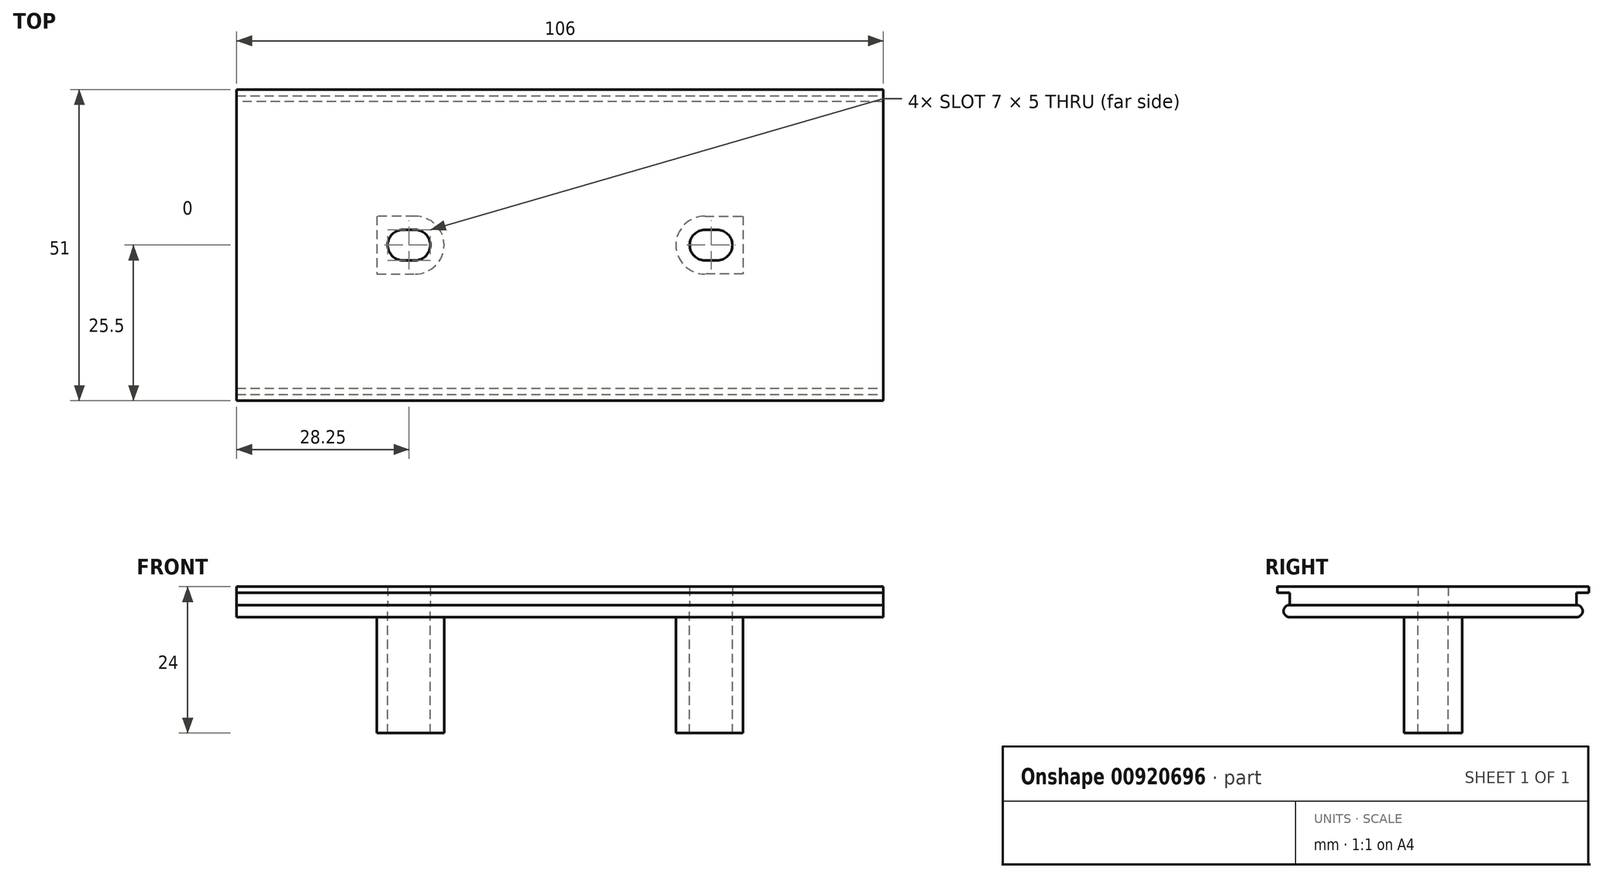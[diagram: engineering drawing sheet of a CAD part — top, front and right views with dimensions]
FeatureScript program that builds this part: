
annotation { "Feature Type Name" : "Feature", "Feature Type Description" : "" }
export const myFeature = defineFeature(function(context is Context, id is Id, definition is map)
    precondition{}
    {
        {
            var Q0;
            Q0=qCreatedBy(makeId("Top.planeOp"),FACE);
            var sketch = newSketch(context, id + "F0", { "sketchPlane" : qUnion([Q0])});
            skLineSegment(sketch, "E0", {"start": v(0, 0) * mm, "end": v(106, 0) * mm});
            skLineSegment(sketch, "E1", {"start": v(106, 0) * mm, "end": v(106, 47) * mm});
            skLineSegment(sketch, "E2", {"start": v(106, 47) * mm, "end": v(0, 47) * mm});
            skLineSegment(sketch, "E3", {"start": v(0, 47) * mm, "end": v(0, 0) * mm});
            skSolve(sketch);
        }
        {
            var Q0;
            Q0=makeQuery(id+"F0.imprint","IMPRINT",FACE,{"disambiguationData":[TD([[makeQuery(id+"F0.imprint","IMPRINT",EDGE,{"derivedFrom":sQuery(id+"F0.wireOp",EDGE,"E0")}),1.0]])]});
            extrude(context, id + "F1", {"entities" : qUnion([Q0]), "depth" : 2 * mm, "offsetDistance" : 25 * mm});
        }
        {
            var Q0;
            Q0=makeQuery(id+"F1.opExtrude","CAP_FACE",FACE,{"disambiguationData":[OSD([sQuery(id+"F0.wireOp",EDGE,"E0"),sQuery(id+"F0.wireOp",EDGE,"E1"),sQuery(id+"F0.wireOp",EDGE,"E2"),sQuery(id+"F0.wireOp",EDGE,"E3")])],"isStart":false});
            var sketch = newSketch(context, id + "F2", { "sketchPlane" : qUnion([Q0])});
            skLineSegment(sketch, "E4", {"start": v(0, 0) * mm, "end": v(0, -2) * mm});
            skLineSegment(sketch, "E5", {"start": v(0, -2) * mm, "end": v(106, -2) * mm});
            skLineSegment(sketch, "E6", {"start": v(106, -2) * mm, "end": v(106, 49) * mm});
            skLineSegment(sketch, "E7", {"start": v(106, 49) * mm, "end": v(0, 49) * mm});
            skLineSegment(sketch, "E8", {"start": v(0, 49) * mm, "end": v(0, -2) * mm});
            skSolve(sketch);
        }
        {
            var Q0;
            Q0 = qSketchRegion(id + "F2", true);
            extrude(context, id + "F3", {"entities" : qUnion([Q0]), "operationType" : NewBodyOperationType.ADD, "depth" : 1 * mm, "offsetDistance" : 25 * mm});
        }
        {
            var Q0;
            Q0=makeQuery(id+"F3.boolean.opBoolean","MERGE",FACE,{"derivedFrom":[makeQuery(id+"F1.opExtrude","SWEPT_FACE",FACE,{"disambiguationData":[OSD([sQuery(id+"F0.wireOp",EDGE,"E1")])]}),makeQuery(id+"F3.opExtrude","SWEPT_FACE",FACE,{"disambiguationData":[OSD([sQuery(id+"F2.wireOp",EDGE,"E6")])]})]});
            var sketch = newSketch(context, id + "F4", { "sketchPlane" : qUnion([Q0])});
            skArc(sketch, "E9", {"start": v(0, 0) * mm, "mid": v(-1, -1) * mm, "end": v(0, -2) * mm});
            skLineSegment(sketch, "E10", {"start": v(23.5, 3) * mm, "end": v(23.5, -3.76) * mm, "construction": true});
            skArc(sketch, "E11.MirrorCS", {"start": v(47, 0) * mm, "mid": v(48, -1) * mm, "end": v(47, -2) * mm});
            skLineSegment(sketch, "E12", {"start": v(0, -2) * mm, "end": v(47, -2) * mm});
            skSolve(sketch);
        }
        {
            var Q0;
            Q0=makeQuery(id+"F4.imprint","IMPRINT",FACE,{"disambiguationData":[TD([[makeQuery(id+"F4.imprint","IMPRINT",EDGE,{"derivedFrom":sQuery(id+"F4.wireOp",EDGE,"E9")}),1.0]])]});
            extrude(context, id + "F5", {"entities" : qUnion([Q0]), "oppositeDirection" : true, "depth" : 106 * mm, "offsetDistance" : 25 * mm});
        }
        {
            var Q0;
            Q0=makeQuery(id+"F5.opExtrude","SWEPT_FACE",FACE,{"disambiguationData":[OSD([sQuery(id+"F4.wireOp",EDGE,"E12")])]});
            var sketch = newSketch(context, id + "F6", { "sketchPlane" : qUnion([Q0])});
            skArc(sketch, "E13", {"start": v(76.75, -18.75) * mm, "mid": v(72, -23.5) * mm, "end": v(76.75, -28.25) * mm});
            skLineSegment(sketch, "E14", {"start": v(76.75, -28.25) * mm, "end": v(83, -28.25) * mm});
            skLineSegment(sketch, "E15", {"start": v(83, -28.25) * mm, "end": v(83, -18.75) * mm});
            skLineSegment(sketch, "E16", {"start": v(83, -18.75) * mm, "end": v(76.75, -18.75) * mm});
            skLineSegment(sketch, "E17", {"start": v(53, 0) * mm, "end": v(53, -47) * mm, "construction": true});
            skLineSegment(sketch, "E18.MirrorCS", {"start": v(29.25, -28.25) * mm, "end": v(23, -28.25) * mm});
            skLineSegment(sketch, "E19.MirrorCS", {"start": v(23, -28.25) * mm, "end": v(23, -18.75) * mm});
            skLineSegment(sketch, "E20.MirrorCS", {"start": v(23, -18.75) * mm, "end": v(29.25, -18.75) * mm});
            skArc(sketch, "E21.MirrorCS", {"start": v(29.25, -18.75) * mm, "mid": v(34, -23.5) * mm, "end": v(29.25, -28.25) * mm});
            skLineSegment(sketch, "E22", {"start": v(0, -23.5) * mm, "end": v(106, -23.5) * mm, "construction": true});
            skArc(sketch, "E23", {"start": v(76.75, -21) * mm, "mid": v(74.25, -23.5) * mm, "end": v(76.75, -26) * mm});
            skArc(sketch, "E24", {"start": v(78.75, -26) * mm, "mid": v(81.25, -23.5) * mm, "end": v(78.75, -21) * mm});
            skLineSegment(sketch, "E25", {"start": v(76.75, -21) * mm, "end": v(78.75, -21) * mm});
            skLineSegment(sketch, "E26", {"start": v(78.75, -26) * mm, "end": v(76.75, -26) * mm});
            skArc(sketch, "E27.MirrorCS", {"start": v(29.25, -21) * mm, "mid": v(31.75, -23.5) * mm, "end": v(29.25, -26) * mm});
            skLineSegment(sketch, "E28.MirrorCS", {"start": v(29.25, -21) * mm, "end": v(27.25, -21) * mm});
            skArc(sketch, "E29.MirrorCS", {"start": v(27.25, -26) * mm, "mid": v(24.75, -23.5) * mm, "end": v(27.25, -21) * mm});
            skLineSegment(sketch, "E30.MirrorCS", {"start": v(27.25, -26) * mm, "end": v(29.25, -26) * mm});
            skSolve(sketch);
        }
        {
            var Q0;
            Q0=makeQuery(id+"F6.imprint","IMPRINT",FACE,{"disambiguationData":[TD([[makeQuery(id+"F6.imprint","IMPRINT",EDGE,{"derivedFrom":sQuery(id+"F6.wireOp",EDGE,"E18.MirrorCS")}),-1.0]])]});
            var Q1;
            Q1=makeQuery(id+"F6.imprint","IMPRINT",FACE,{"disambiguationData":[TD([[makeQuery(id+"F6.imprint","IMPRINT",EDGE,{"derivedFrom":sQuery(id+"F6.wireOp",EDGE,"E13")}),1.0]])]});
            extrude(context, id + "F7", {"entities" : qUnion([Q0, Q1]), "operationType" : NewBodyOperationType.ADD, "depth" : 19 * mm, "offsetDistance" : 25 * mm});
        }
        {
            var Q0;
            Q0=makeQuery(id+"F7.boolean.opBoolean","SPLIT",FACE,{"disambiguationData":[TD([makeQuery(id+"F7.opExtrude","SWEPT_FACE",FACE,{"disambiguationData":[OSD([sQuery(id+"F6.wireOp",EDGE,"E27.MirrorCS")])]})])],"derivedFrom":makeQuery(id+"F5.opExtrude","SWEPT_FACE",FACE,{"disambiguationData":[OSD([sQuery(id+"F4.wireOp",EDGE,"E12")])]})});
            var Q1;
            Q1=makeQuery(id+"F7.boolean.opBoolean","SPLIT",FACE,{"disambiguationData":[TD([makeQuery(id+"F7.opExtrude","SWEPT_FACE",FACE,{"disambiguationData":[OSD([sQuery(id+"F6.wireOp",EDGE,"E23")])]})])],"derivedFrom":makeQuery(id+"F5.opExtrude","SWEPT_FACE",FACE,{"disambiguationData":[OSD([sQuery(id+"F4.wireOp",EDGE,"E12")])]})});
            extrude(context, id + "F8", {"entities" : qUnion([Q0, Q1]), "operationType" : NewBodyOperationType.REMOVE, "oppositeDirection" : true, "depth" : 25 * mm, "offsetDistance" : 25 * mm});
        }
    });
